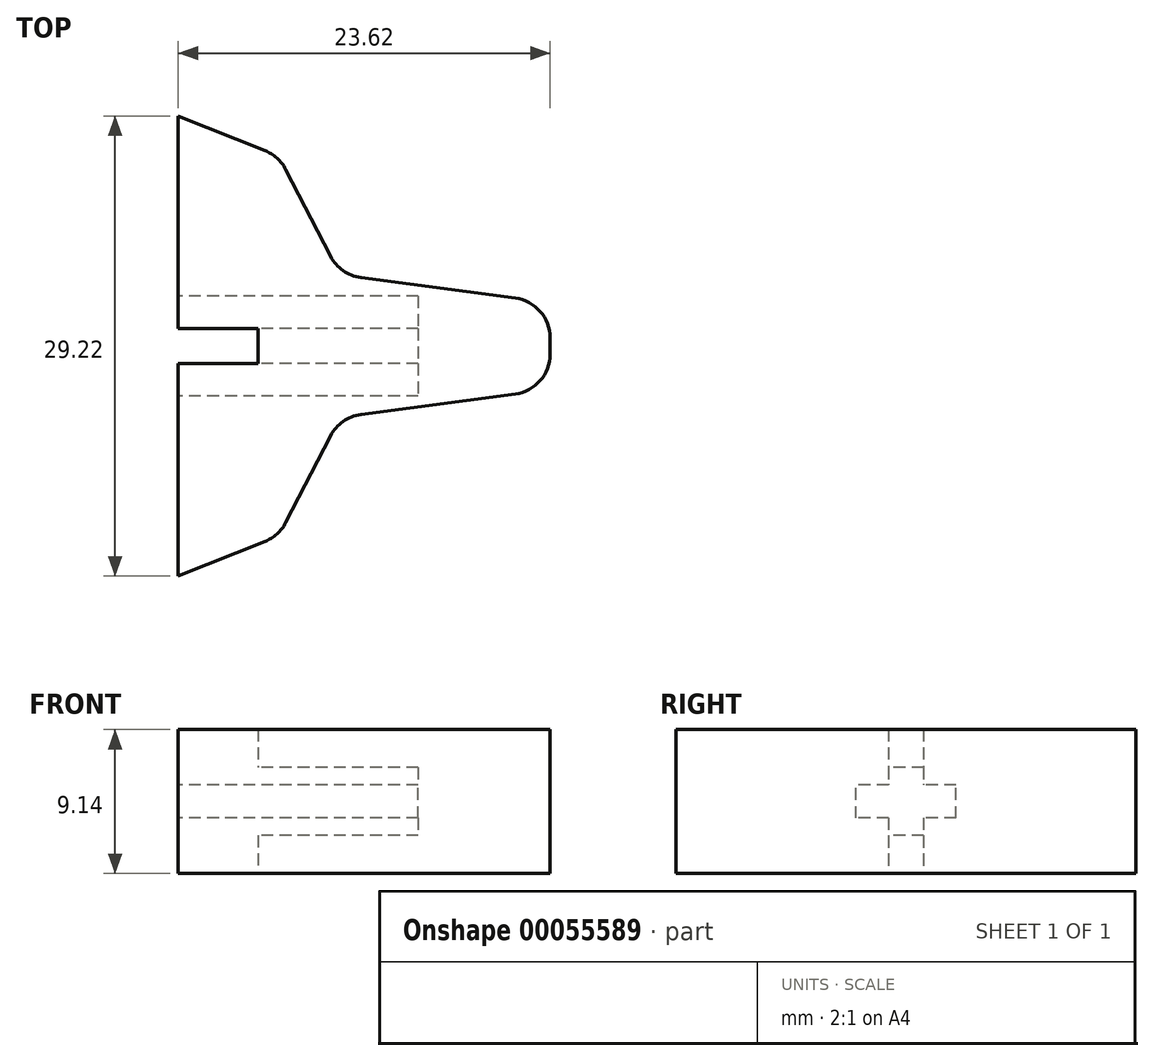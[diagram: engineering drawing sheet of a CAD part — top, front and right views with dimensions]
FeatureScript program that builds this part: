
annotation { "Feature Type Name" : "Feature", "Feature Type Description" : "" }
export const myFeature = defineFeature(function(context is Context, id is Id, definition is map)
    precondition{}
    {
        {
            var Q0;
            Q0=qCreatedBy(makeId("Top.planeOp"),FACE);
            var sketch = newSketch(context, id + "F0", { "sketchPlane" : qUnion([Q0])});
            skLineSegment(sketch, "E0.bottom", {"start": v(0, 14.6) * mm, "end": v(23.62, 14.6) * mm});
            skLineSegment(sketch, "E0.top", {"start": v(0, -14.6) * mm, "end": v(23.62, -14.6) * mm});
            skLineSegment(sketch, "E0.left", {"start": v(0, 14.6) * mm, "end": v(0, -14.6) * mm});
            skLineSegment(sketch, "E0.right", {"start": v(23.62, 14.6) * mm, "end": v(23.62, -14.6) * mm});
            skLineSegment(sketch, "E1", {"start": v(10.29, 14.6) * mm, "end": v(10.29, -14.6) * mm});
            skLineSegment(sketch, "E2", {"start": v(23.62, 2.75) * mm, "end": v(10.29, 4.52) * mm});
            skLineSegment(sketch, "E3", {"start": v(0, 0) * mm, "end": v(23.62, 0) * mm, "construction": true});
            skLineSegment(sketch, "E4", {"start": v(10.29, 4.52) * mm, "end": v(5.08, 14.6) * mm});
            skLineSegment(sketch, "E5", {"start": v(0, 14.6) * mm, "end": v(6.4, 12.06) * mm});
            skLineSegment(sketch, "E6.MirrorCS", {"start": v(0, -14.6) * mm, "end": v(6.4, -12.06) * mm});
            skLineSegment(sketch, "E7.MirrorCS", {"start": v(10.29, -4.52) * mm, "end": v(5.08, -14.6) * mm});
            skLineSegment(sketch, "E8.MirrorCS", {"start": v(23.62, -2.75) * mm, "end": v(10.29, -4.52) * mm});
            skSolve(sketch);
        }
        {
            var Q0;
            {var subQ0=sQuery(id+"F0.wireOp",EDGE,"E2");Q0=makeQuery(id+"F0.imprint","IMPRINT",FACE,{"disambiguationData":[TD([[makeQuery(id+"F0.imprint","IMPRINT",EDGE,{"derivedFrom":subQ0}),1.0]])]});}
            var Q1;
            Q1=makeQuery(id+"F0.imprint","IMPRINT",FACE,{"disambiguationData":[TD([[makeQuery(id+"F0.imprint","IMPRINT",EDGE,{"derivedFrom":sQuery(id+"F0.wireOp",EDGE,"E0.left")}),1.0]])]});
            extrude(context, id + "F1", {"entities" : qUnion([Q0, Q1]), "depth" : 9.14 * mm});
        }
        {
            var Q0;
            Q0=makeQuery(id+"F1.opExtrude","SWEPT_FACE",FACE,{"disambiguationData":[OSD([sQuery(id+"F0.wireOp",EDGE,"E0.left")])]});
            var sketch = newSketch(context, id + "F2", { "sketchPlane" : qUnion([Q0])});
            skLineSegment(sketch, "E9.rect.bottom", {"start": v(-3.18, 3.52) * mm, "end": v(3.17, 3.52) * mm});
            skLineSegment(sketch, "E9.rect.top", {"start": v(-3.18, 5.62) * mm, "end": v(3.17, 5.62) * mm});
            skLineSegment(sketch, "E9.rect.left", {"start": v(-3.18, 3.52) * mm, "end": v(-3.18, 5.62) * mm});
            skLineSegment(sketch, "E9.rect.right", {"start": v(3.17, 3.52) * mm, "end": v(3.17, 5.62) * mm});
            skPoint(sketch, "E9.rect.middle", {"position": v(0, 4.57) * mm});
            skPoint(sketch, "E9.rect.middle.positionSnap0", {"position": v(-14.6, 4.57) * mm});
            skPoint(sketch, "E9.rect.middle.positionSnap1", {"position": v(0, 9.14) * mm});
            skPoint(sketch, "E9.rect.centerSnap0", {"position": v(-14.6, 4.57) * mm});
            skPoint(sketch, "E9.rect.centerSnap1", {"position": v(0, 9.14) * mm});
            skLineSegment(sketch, "E10.rect.bottom", {"start": v(-1.11, 9.14) * mm, "end": v(1.11, 9.14) * mm});
            skLineSegment(sketch, "E10.rect.top", {"start": v(-1.11, 0) * mm, "end": v(1.11, 0) * mm});
            skLineSegment(sketch, "E10.rect.left", {"start": v(-1.11, 9.14) * mm, "end": v(-1.11, 0) * mm});
            skLineSegment(sketch, "E10.rect.right", {"start": v(1.11, 9.14) * mm, "end": v(1.11, 0) * mm});
            skLineSegment(sketch, "E11.rect.bottom", {"start": v(-1.11, 6.73) * mm, "end": v(1.11, 6.73) * mm});
            skLineSegment(sketch, "E11.rect.top", {"start": v(-1.11, 2.41) * mm, "end": v(1.11, 2.41) * mm});
            skLineSegment(sketch, "E11.rect.left", {"start": v(-1.11, 6.73) * mm, "end": v(-1.11, 2.41) * mm});
            skLineSegment(sketch, "E11.rect.right", {"start": v(1.11, 6.73) * mm, "end": v(1.11, 2.41) * mm});
            skSolve(sketch);
        }
        {
            var Q0;
            Q0 = qSketchRegion(id + "F2", true);
            extrude(context, id + "F3", {"entities" : qUnion([Q0]), "operationType" : NewBodyOperationType.REMOVE, "oppositeDirection" : true, "depth" : 5.08 * mm});
        }
        {
            var Q0;
            {var subQ5=sQuery(id+"F2.wireOp",EDGE,"E11.rect.top");Q0=makeQuery(id+"F2.imprint","IMPRINT",FACE,{"disambiguationData":[TD([[makeQuery(id+"F2.imprint","IMPRINT",EDGE,{"derivedFrom":subQ5}),1.0]])]});}
            var Q1;
            {var subQ0=sQuery(id+"F2.wireOp",EDGE,"E11.rect.left");var subQ1=sQuery(id+"F2.wireOp",EDGE,"E9.rect.bottom");var subQ2=makeQuery(id+"F2.imprint","INTERSECT",VERTEX,{"derivedFrom":[subQ1,subQ0]});Q1=makeQuery(id+"F2.imprint","IMPRINT",FACE,{"disambiguationData":[TD([[makeQuery(id+"F2.imprint","IMPRINT",EDGE,{"disambiguationData":[TD([[subQ2,-1.0]])],"derivedFrom":subQ1}),1.0]])]});}
            var Q2;
            {var subQ5=sQuery(id+"F2.wireOp",EDGE,"E11.rect.bottom");Q2=makeQuery(id+"F2.imprint","IMPRINT",FACE,{"disambiguationData":[TD([[makeQuery(id+"F2.imprint","IMPRINT",EDGE,{"derivedFrom":subQ5}),-1.0]])]});}
            extrude(context, id + "F4", {"entities" : qUnion([Q0, Q1, Q2]), "operationType" : NewBodyOperationType.REMOVE, "oppositeDirection" : true, "depth" : 15.24 * mm});
        }
        {
            var Q0;
            Q0=makeQuery(id+"F1.opExtrude","SWEPT_EDGE",EDGE,{"disambiguationData":[OSD([sQuery(id+"F0.wireOp",EDGE,"E0.right"),sQuery(id+"F0.wireOp",EDGE,"E2")])]});
            var Q1;
            Q1=makeQuery(id+"F1.opExtrude","SWEPT_EDGE",EDGE,{"disambiguationData":[OSD([sQuery(id+"F0.wireOp",EDGE,"E0.right"),sQuery(id+"F0.wireOp",EDGE,"E8.MirrorCS")])]});
            var Q2;
            Q2=makeQuery(id+"F1.opExtrude","SWEPT_EDGE",EDGE,{"disambiguationData":[OSD([sQuery(id+"F0.wireOp",EDGE,"E1"),sQuery(id+"F0.wireOp",EDGE,"E2"),sQuery(id+"F0.wireOp",EDGE,"E4")])]});
            var Q3;
            Q3=makeQuery(id+"F1.opExtrude","SWEPT_EDGE",EDGE,{"disambiguationData":[OSD([sQuery(id+"F0.wireOp",EDGE,"E4"),sQuery(id+"F0.wireOp",EDGE,"E5")])]});
            var Q4;
            Q4=makeQuery(id+"F1.opExtrude","SWEPT_EDGE",EDGE,{"disambiguationData":[OSD([sQuery(id+"F0.wireOp",EDGE,"E1"),sQuery(id+"F0.wireOp",EDGE,"E7.MirrorCS"),sQuery(id+"F0.wireOp",EDGE,"E8.MirrorCS")])]});
            var Q5;
            Q5=makeQuery(id+"F1.opExtrude","SWEPT_EDGE",EDGE,{"disambiguationData":[OSD([sQuery(id+"F0.wireOp",EDGE,"E6.MirrorCS"),sQuery(id+"F0.wireOp",EDGE,"E7.MirrorCS")])]});
            fillet(context, id + "F5", {"entities" : qUnion([Q0, Q1, Q2, Q3, Q4, Q5]), "radius" : 2.54 * mm, "tangentPropagation" : true, "allowEdgeOverflow" : false});
        }
    });
